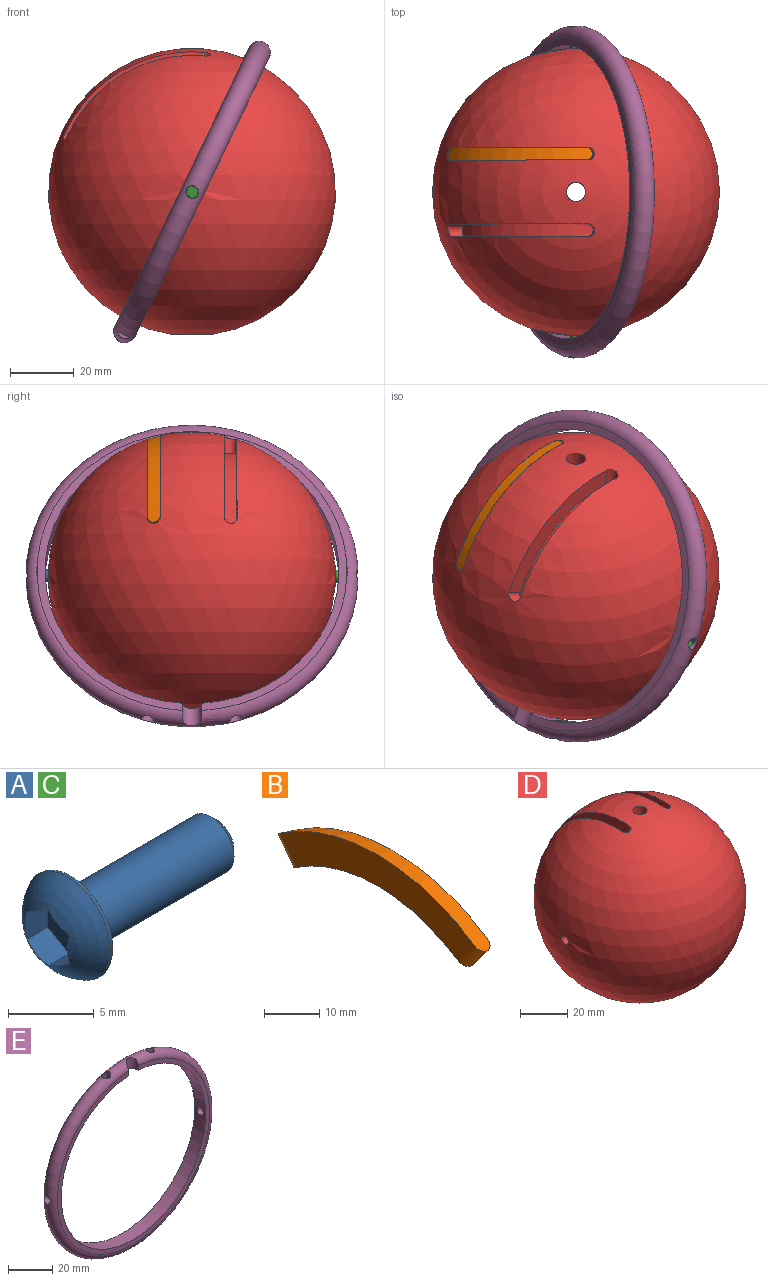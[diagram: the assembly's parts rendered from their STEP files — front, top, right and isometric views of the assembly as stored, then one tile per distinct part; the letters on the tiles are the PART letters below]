
ASSEMBLY  parts=5 mates=5
PART A: 13 faces, bbox 14.1x7.6x7.6 mm
  f0: plane 6.6x6.6mm, normal (1,0,0), area 22.9mm2, adj f3,f4
  f1: sphere r=3.84mm, area 42.3mm2, adj f4,f6,f7,f8,f9,f10,f11
  f2: plane 2.8x2.8mm, normal (1,0,0), area 6.2mm2, adj f5
  f3: cylinder r=1.9mm len=11.5mm, axis (-1,0,0), area 137.3mm2, adj f0,f5
  f4: torus R=3.3mm, axis (1,0,0), area 8.7mm2, adj f0,f1
  f5: cone r=1.9mm half-angle=45deg, axis (-1,0,0), area 7.3mm2, adj f2,f3
  f6: plane 1.88x1.75mm, normal (0,-0.5,-0.87), area 3.7mm2, adj f1,f7,f11,f12
  f7: plane 2.02x1.88mm, normal (0,-1,0), area 3.7mm2, adj f1,f6,f8,f12
  f8: plane 1.88x1.75mm, normal (0,-0.5,0.87), area 3.7mm2, adj f1,f7,f9,f12
  f9: plane 1.88x1.75mm, normal (0,0.5,0.87), area 3.7mm2, adj f1,f8,f10,f12
  f10: plane 2.02x1.88mm, normal (0,1,0), area 3.7mm2, adj f1,f9,f11,f12
  f11: plane 1.88x1.75mm, normal (0,0.5,-0.87), area 3.7mm2, adj f1,f6,f10,f12
  f12: plane 4.04x3.5mm, normal (-1,0,0), area 10.6mm2, adj f6,f7,f8,f9,f10,f11
PART B: 6 faces, bbox 4x52.8x14.4 mm
  f0: sphere r=45mm, area 228.9mm2, adj f1,f3,f4,f5
  f1: plane 49.56x13.17mm, normal (-1,0,0), area 331.5mm2, adj f0,f2,f4,f5
  f2: cylinder r=37mm len=44.53mm, axis (1,0,0), area 187.7mm2, adj f1,f3,f4,f5
  f3: plane 48.22x12.06mm, normal (1,0,0), area 274mm2, adj f0,f2,f4,f5
  f4: cylinder r=2mm len=6.71mm, axis (0,-0.6,0.8), area 39.9mm2, adj f0,f1,f2,f3
  f5: cylinder r=2mm len=6.71mm, axis (0,0.6,0.8), area 39.9mm2, adj f0,f1,f2,f3
PART C: same geometry as A
PART D: 16 faces, bbox 90.4x90.4x89.9 mm
  f0: sphere r=45mm, area 24814.1mm2, adj f1,f2,f3,f5,f6,f7,f8,f10
  f1: cylinder r=3mm len=79.9mm, axis (0,0,1), area 1479.2mm2, adj f0,f2,f3,f14
  f2: cylinder r=2mm len=41.96mm, axis (1,0,0), area 527.2mm2, adj f0,f1
  f3: cylinder r=2mm len=41.96mm, axis (1,0,0), area 527.2mm2, adj f0,f1
  f4: cylinder r=38.37mm len=40.91mm, axis (1,0,0), area 200.1mm2, adj f5,f6,f7,f8
  f5: plane 43.97x28.04mm, normal (1,0,0), area 276.5mm2, adj f0,f4,f7,f8
  f6: plane 42.75x26.81mm, normal (-1,0,0), area 217.9mm2, adj f0,f4,f7,f8
  f7: cylinder r=2mm len=5.66mm, axis (0,-0.09,1), area 31.1mm2, adj f0,f4,f5,f6
  f8: cylinder r=2mm len=5.83mm, axis (0,0.91,0.42), area 31.1mm2, adj f0,f4,f5,f6
  f9: cylinder r=38.37mm len=40.91mm, axis (-1,0,0), area 200.1mm2, adj f10,f11,f12,f13
  f10: plane 43.59x27.66mm, normal (-1,0,0), area 276.5mm2, adj f0,f9,f12,f13
  f11: plane 42.49x26.55mm, normal (1,0,0), area 217.9mm2, adj f0,f9,f12,f13
  f12: cylinder r=2mm len=5.66mm, axis (0,-0.09,1), area 31.1mm2, adj f0,f9,f10,f11
  f13: cylinder r=2mm len=5.83mm, axis (0,0.91,0.42), area 31.1mm2, adj f0,f9,f10,f11
  f14: plane 12x12mm, normal (0,0,-1), area 84.8mm2, adj f1,f15
  f15: cylinder r=6mm len=12mm, axis (0,0,1), area 361.8mm2, adj f0,f14
PART E: 11 faces, bbox 112.6x7x112.6 mm
  f0: cylinder r=46mm len=92mm, axis (0,1,0), area 1953.6mm2, adj f2,f3,f4,f5,f6,f7,f8,f9
  f1: torus R=48.5mm, axis (0,-1,0), area 3420.7mm2, adj f2,f3,f4,f5,f6,f7,f8,f9
  f2: plane 97x96.91mm, normal (0,-1,0), area 727.2mm2, adj f0,f1,f7,f8
  f3: cylinder r=3mm len=6.1mm, axis (0,0,-1), area 53.4mm2, adj f0,f1,f7,f8
  f4: plane 97x97mm, normal (0,1,0), area 742.2mm2, adj f0,f1
  f5: cylinder r=2mm len=6.01mm, axis (1,0,0), area 71.6mm2, adj f0,f1
  f6: cylinder r=2mm len=6.01mm, axis (1,0,0), area 71.6mm2, adj f0,f1
  f7: plane 4.32x0.51mm, normal (-1,0,0), area 1.9mm2, adj f0,f1,f2,f3
  f8: plane 4.32x0.51mm, normal (1,0,0), area 1.9mm2, adj f0,f1,f2,f3
  f9: cylinder r=2.1mm len=6.91mm, axis (-0.27,0,-0.96), area 74.7mm2, adj f0,f1
  f10: cylinder r=2.1mm len=6.91mm, axis (0.27,0,-0.96), area 74.7mm2, adj f0,f1
PLACE A rot(axis=(0,0,-1),89.9deg) t=(-3.77,49.62,-6.34)mm
PLACE B rot(axis=(-0.25,-0.25,0.93),94deg) t=(-3.67,1.12,-6.37)mm
PLACE C rot(axis=(0.67,0.67,0.31),145.6deg) t=(-3.57,-47.38,-6.39)mm
PLACE D rot(axis=(0,0,1),90.1deg) t=(-3.67,1.12,-6.37)mm fixed
PLACE E rot(axis=(-0.7,-0.7,0.16),161.9deg) t=(-3.67,1.12,-6.37)mm
MATE planar D.f6 <-> B.f3  axis (0,-1,0) through (-22.76,15.06,26.66)mm
MATE cylindrical D.f2 <-> A.f4  axis (0,1,0) through (-3.66,-0.85,-6.37)mm
MATE ball D.f1 <-> E.f0  axis (0,0,1) through (-3.67,1.12,-6.37)mm
MATE cylindrical A.f3 <-> E.f5  axis (0,1,0) through (-3.74,38.12,-6.35)mm
MATE cylindrical D.f4 <-> B.f2  axis (0,1,0) through (-3.69,13.12,-6.36)mm
